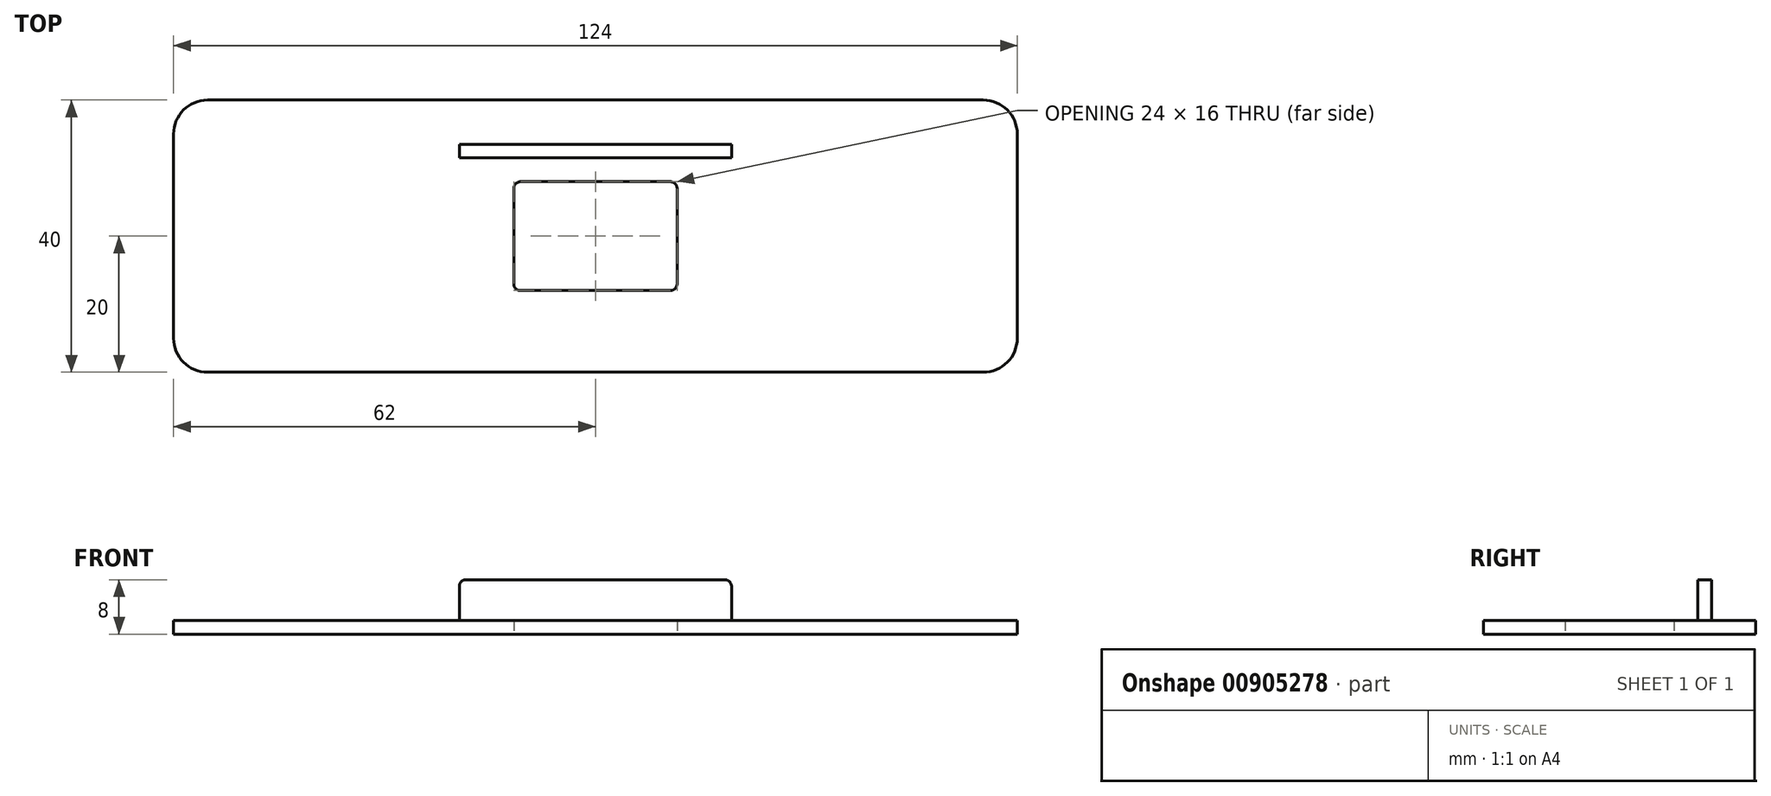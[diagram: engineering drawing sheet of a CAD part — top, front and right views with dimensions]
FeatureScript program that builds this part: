
annotation { "Feature Type Name" : "Feature", "Feature Type Description" : "" }
export const myFeature = defineFeature(function(context is Context, id is Id, definition is map)
    precondition{}
    {
        {
            var Q0;
            Q0=qCreatedBy(makeId("Top.planeOp"),FACE);
            var sketch = newSketch(context, id + "F0", { "sketchPlane" : qUnion([Q0])});
            skLineSegment(sketch, "E0.bottom", {"start": v(12, -8) * mm, "end": v(-12, -8) * mm});
            skLineSegment(sketch, "E0.top", {"start": v(12, 8) * mm, "end": v(-12, 8) * mm});
            skLineSegment(sketch, "E0.left", {"start": v(12, -8) * mm, "end": v(12, 8) * mm});
            skLineSegment(sketch, "E0.right", {"start": v(-12, -8) * mm, "end": v(-12, 8) * mm});
            skPoint(sketch, "E0.middle", {"position": v(0, 0) * mm});
            skLineSegment(sketch, "E1.bottom", {"start": v(62, -20) * mm, "end": v(-62, -20) * mm});
            skLineSegment(sketch, "E1.top", {"start": v(62, 20) * mm, "end": v(-62, 20) * mm});
            skLineSegment(sketch, "E1.left", {"start": v(62, -20) * mm, "end": v(62, 20) * mm});
            skLineSegment(sketch, "E1.right", {"start": v(-62, -20) * mm, "end": v(-62, 20) * mm});
            skLineSegment(sketch, "E2.bottom", {"start": v(20, 11.5) * mm, "end": v(-20, 11.5) * mm});
            skLineSegment(sketch, "E2.top", {"start": v(20, 13.5) * mm, "end": v(-20, 13.5) * mm});
            skLineSegment(sketch, "E2.left", {"start": v(20, 11.5) * mm, "end": v(20, 13.5) * mm});
            skLineSegment(sketch, "E2.right", {"start": v(-20, 11.5) * mm, "end": v(-20, 13.5) * mm});
            skPoint(sketch, "E2.middle", {"position": v(0, 12.5) * mm});
            skSolve(sketch);
        }
        {
            var Q0;
            Q0=makeQuery(id+"F0.imprint","IMPRINT",FACE,{"disambiguationData":[TD([[makeQuery(id+"F0.imprint","IMPRINT",EDGE,{"derivedFrom":sQuery(id+"F0.wireOp",EDGE,"E0.bottom")}),1.0]])]});
            extrude(context, id + "F1", {"entities" : qUnion([Q0]), "depth" : 2 * mm, "offsetDistance" : 25 * mm});
        }
        {
            var Q0;
            Q0=makeQuery(id+"F1.opExtrude","SWEPT_EDGE",EDGE,{"disambiguationData":[OSD([sQuery(id+"F0.wireOp",EDGE,"E1.top"),sQuery(id+"F0.wireOp",EDGE,"E1.right")])]});
            var Q1;
            Q1=makeQuery(id+"F1.opExtrude","SWEPT_EDGE",EDGE,{"disambiguationData":[OSD([sQuery(id+"F0.wireOp",EDGE,"E1.top"),sQuery(id+"F0.wireOp",EDGE,"E1.left")])]});
            var Q2;
            Q2=makeQuery(id+"F1.opExtrude","SWEPT_EDGE",EDGE,{"disambiguationData":[OSD([sQuery(id+"F0.wireOp",EDGE,"E1.bottom"),sQuery(id+"F0.wireOp",EDGE,"E1.left")])]});
            var Q3;
            Q3=makeQuery(id+"F1.opExtrude","SWEPT_EDGE",EDGE,{"disambiguationData":[OSD([sQuery(id+"F0.wireOp",EDGE,"E1.bottom"),sQuery(id+"F0.wireOp",EDGE,"E1.right")])]});
            fillet(context, id + "F2", {"entities" : qUnion([Q0, Q1, Q2, Q3]), "radius" : 5 * mm, "tangentPropagation" : true, "allowEdgeOverflow" : false});
        }
        {
            var Q0;
            Q0=makeQuery(id+"F1.opExtrude","SWEPT_EDGE",EDGE,{"disambiguationData":[OSD([sQuery(id+"F0.wireOp",EDGE,"E0.bottom"),sQuery(id+"F0.wireOp",EDGE,"E0.left")])]});
            var Q1;
            Q1=makeQuery(id+"F1.opExtrude","SWEPT_EDGE",EDGE,{"disambiguationData":[OSD([sQuery(id+"F0.wireOp",EDGE,"E0.bottom"),sQuery(id+"F0.wireOp",EDGE,"E0.right")])]});
            var Q2;
            Q2=makeQuery(id+"F1.opExtrude","SWEPT_EDGE",EDGE,{"disambiguationData":[OSD([sQuery(id+"F0.wireOp",EDGE,"E0.top"),sQuery(id+"F0.wireOp",EDGE,"E0.left")])]});
            var Q3;
            Q3=makeQuery(id+"F1.opExtrude","SWEPT_EDGE",EDGE,{"disambiguationData":[OSD([sQuery(id+"F0.wireOp",EDGE,"E0.top"),sQuery(id+"F0.wireOp",EDGE,"E0.right")])]});
            fillet(context, id + "F3", {"entities" : qUnion([Q0, Q1, Q2, Q3]), "radius" : 1 * mm, "tangentPropagation" : true, "allowEdgeOverflow" : false});
        }
        {
            var Q0;
            Q0=makeQuery(id+"F0.imprint","IMPRINT",FACE,{"disambiguationData":[TD([[makeQuery(id+"F0.imprint","IMPRINT",EDGE,{"derivedFrom":sQuery(id+"F0.wireOp",EDGE,"E2.bottom")}),-1.0]])]});
            extrude(context, id + "F4", {"entities" : qUnion([Q0]), "operationType" : NewBodyOperationType.ADD, "depth" : 8 * mm, "offsetDistance" : 25 * mm});
        }
        {
            var Q0;
            Q0=makeQuery(id+"F1.opExtrude","CAP_EDGE",EDGE,{"disambiguationData":[OSD([sQuery(id+"F0.wireOp",EDGE,"E2.top")])],"isStart":false});
            var Q1;
            Q1=makeQuery(id+"F4.opExtrude","CAP_EDGE",EDGE,{"disambiguationData":[OSD([sQuery(id+"F0.wireOp",EDGE,"E2.left")])],"isStart":false});
            var Q2;
            Q2=makeQuery(id+"F4.opExtrude","CAP_EDGE",EDGE,{"disambiguationData":[OSD([sQuery(id+"F0.wireOp",EDGE,"E2.right")])],"isStart":false});
            fillet(context, id + "F5", {"entities" : qUnion([Q0, Q1, Q2]), "radius" : 1 * mm, "tangentPropagation" : true, "allowEdgeOverflow" : false});
        }
    });
